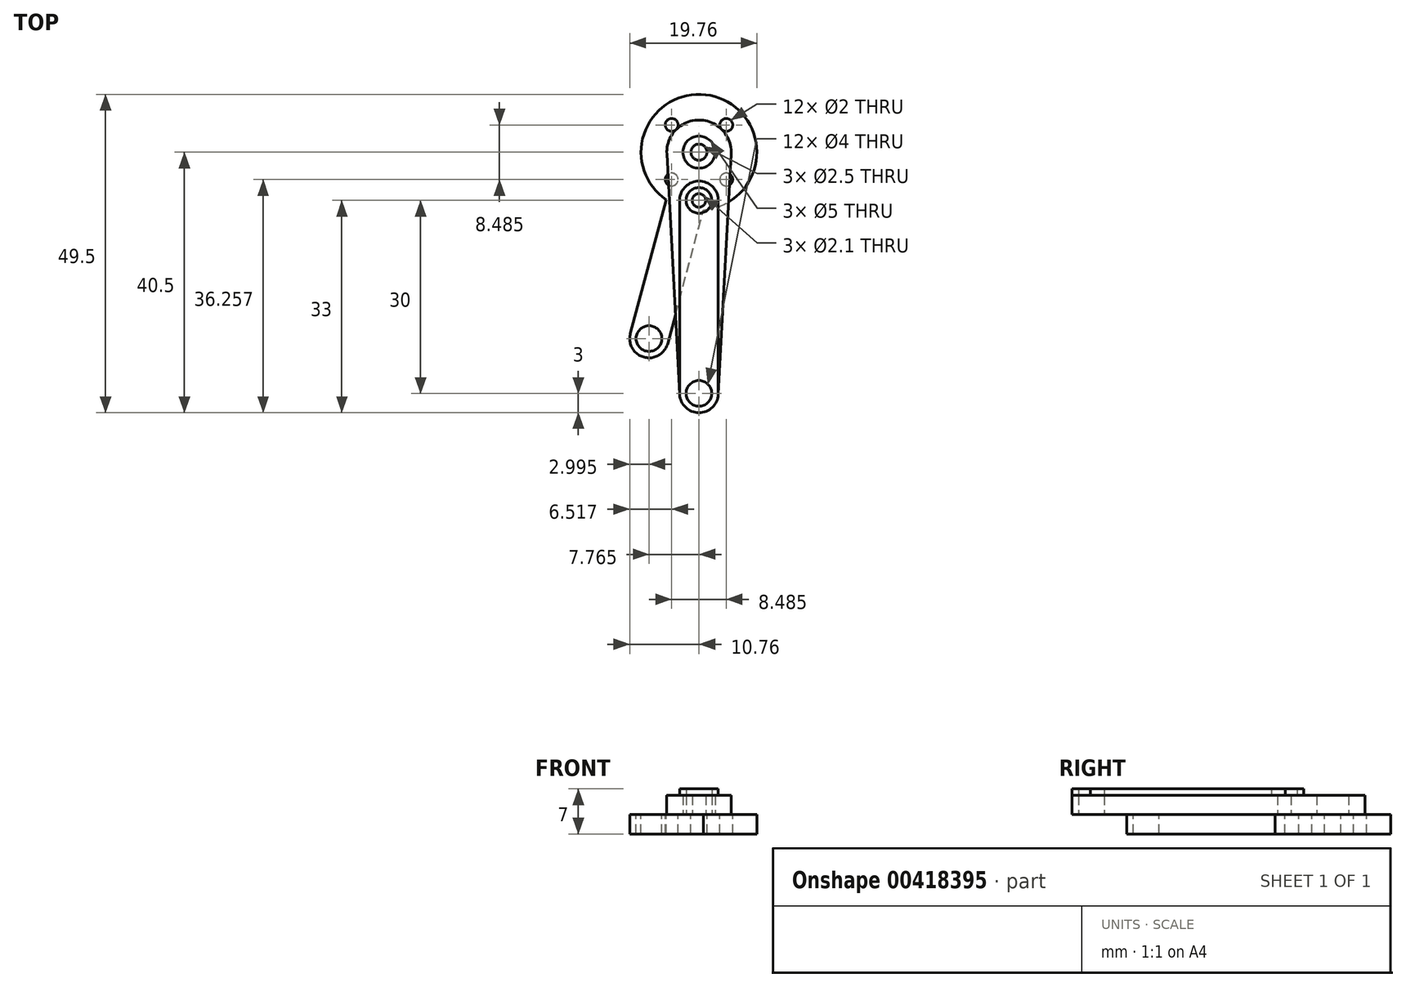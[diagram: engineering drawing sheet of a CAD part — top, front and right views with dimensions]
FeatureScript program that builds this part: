
annotation { "Feature Type Name" : "Feature", "Feature Type Description" : "" }
export const myFeature = defineFeature(function(context is Context, id is Id, definition is map)
    precondition{}
    {
        {
            var Q0;
            Q0=qCreatedBy(makeId("Top.planeOp"),FACE);
            var sketch = newSketch(context, id + "F0", { "sketchPlane" : qUnion([Q0])});
            skArc(sketch, "E0", {"start": v(5, -0.27) * mm, "mid": v(0, 5) * mm, "end": v(-5, -0.27) * mm});
            skCircle(sketch, "E1", {"center": v(0, 0) * mm, "radius": 2.5 * mm});
            skPoint(sketch, "E2", {"position": v(2.5, 0) * mm});
            skPoint(sketch, "E3", {"position": v(5, 0) * mm});
            skArc(sketch, "E4", {"start": v(-3, -37.66) * mm, "mid": v(0, -40.5) * mm, "end": v(3, -37.66) * mm});
            skLineSegment(sketch, "E5", {"start": v(-5, -0.27) * mm, "end": v(-3, -37.66) * mm});
            skCircle(sketch, "E6", {"center": v(0, -37.5) * mm, "radius": 2 * mm});
            skLineSegment(sketch, "E7.MirrorCS", {"start": v(5, -0.27) * mm, "end": v(3, -37.66) * mm});
            skCircle(sketch, "E8", {"center": v(0, -7.5) * mm, "radius": 1.05 * mm});
            skSolve(sketch);
        }
        {
            var Q0;
            Q0=qSketchRegion(id+"F0",true);
            extrude(context, id + "F1", {"entities" : qUnion([Q0]), "depth" : 3 * mm});
        }
        {
            var Q0;
            Q0=makeQuery(id+"F1.opExtrude","CAP_FACE",FACE,{"disambiguationData":[OSD([sQuery(id+"F0.wireOp",EDGE,"E0"),sQuery(id+"F0.wireOp",EDGE,"E1"),sQuery(id+"F0.wireOp",EDGE,"E4"),sQuery(id+"F0.wireOp",EDGE,"E5"),sQuery(id+"F0.wireOp",EDGE,"E6"),sQuery(id+"F0.wireOp",EDGE,"E7.MirrorCS"),sQuery(id+"F0.wireOp",EDGE,"E8")])],"isStart":false});
            var sketch = newSketch(context, id + "F2", { "sketchPlane" : qUnion([Q0])});
            skCircle(sketch, "E9.0", {"center": v(0, -37.5) * mm, "radius": 2 * mm});
            skArc(sketch, "E10.0", {"start": v(-3, -37.66) * mm, "mid": v(0, -40.5) * mm, "end": v(3, -37.66) * mm});
            skCircle(sketch, "E11", {"center": v(0, -7.5) * mm, "radius": 2 * mm});
            skLineSegment(sketch, "E12", {"start": v(0, -7.5) * mm, "end": v(0, -37.5) * mm, "construction": true});
            skLineSegment(sketch, "E13", {"start": v(-3.8, -22.5) * mm, "end": v(3.8, -22.5) * mm, "construction": true});
            skPoint(sketch, "E13.startSnap0", {"position": v(0, -22.5) * mm});
            skArc(sketch, "E14.MirrorCS", {"start": v(-3, -7.34) * mm, "mid": v(0, -4.5) * mm, "end": v(3, -7.34) * mm});
            skLineSegment(sketch, "E15", {"start": v(-3, -7.34) * mm, "end": v(-3, -37.66) * mm});
            skLineSegment(sketch, "E16.MirrorCS", {"start": v(3, -7.34) * mm, "end": v(3, -37.66) * mm});
            skSolve(sketch);
        }
        {
            var Q0;
            Q0=qSketchRegion(id+"F2",true);
            extrude(context, id + "F3", {"entities" : qUnion([Q0]), "depth" : 1 * mm});
        }
        {
            var Q0;
            Q0=makeQuery(id+"F1.opExtrude","CAP_FACE",FACE,{"disambiguationData":[OSD([sQuery(id+"F0.wireOp",EDGE,"E0"),sQuery(id+"F0.wireOp",EDGE,"E1"),sQuery(id+"F0.wireOp",EDGE,"E4"),sQuery(id+"F0.wireOp",EDGE,"E5"),sQuery(id+"F0.wireOp",EDGE,"E6"),sQuery(id+"F0.wireOp",EDGE,"E7.MirrorCS"),sQuery(id+"F0.wireOp",EDGE,"E8")])],"isStart":true});
            var sketch = newSketch(context, id + "F4", { "sketchPlane" : qUnion([Q0])});
            skCircle(sketch, "E17", {"center": v(0, 0) * mm, "radius": 6 * mm, "construction": true});
            skLineSegment(sketch, "E18.bottom", {"start": v(4.24, -4.24) * mm, "end": v(-4.24, -4.24) * mm, "construction": true});
            skLineSegment(sketch, "E18.top", {"start": v(4.24, 4.24) * mm, "end": v(-4.24, 4.24) * mm, "construction": true});
            skLineSegment(sketch, "E18.left", {"start": v(4.24, -4.24) * mm, "end": v(4.24, 4.24) * mm, "construction": true});
            skLineSegment(sketch, "E18.right", {"start": v(-4.24, -4.24) * mm, "end": v(-4.24, 4.24) * mm, "construction": true});
            skCircle(sketch, "E19", {"center": v(4.24, -4.24) * mm, "radius": 1 * mm});
            skCircle(sketch, "E20.MirrorC", {"center": v(-4.24, -4.24) * mm, "radius": 1 * mm});
            skCircle(sketch, "E21.MirrorC", {"center": v(-4.24, 4.24) * mm, "radius": 1 * mm});
            skCircle(sketch, "E22.MirrorC", {"center": v(4.24, 4.24) * mm, "radius": 1 * mm});
            skCircle(sketch, "E23", {"center": v(0, 0) * mm, "radius": 1.25 * mm});
            skArc(sketch, "E24", {"start": v(-5.1, 7.42) * mm, "mid": v(2.33, -8.7) * mm, "end": v(0.7, 8.97) * mm});
            skCircle(sketch, "E25", {"center": v(-7.76, 28.98) * mm, "radius": 2 * mm});
            skLineSegment(sketch, "E26", {"start": v(0, 0) * mm, "end": v(-7.76, 28.98) * mm, "construction": true});
            skArc(sketch, "E27", {"start": v(-4.87, 29.75) * mm, "mid": v(-8.54, 31.88) * mm, "end": v(-10.66, 28.2) * mm});
            skLineSegment(sketch, "E28", {"start": v(-7.76, 28.98) * mm, "end": v(-10.66, 28.2) * mm, "construction": true});
            skLineSegment(sketch, "E29", {"start": v(-10.66, 28.2) * mm, "end": v(-5.1, 7.42) * mm});
            skLineSegment(sketch, "E30.MirrorCS", {"start": v(-4.87, 29.75) * mm, "end": v(0.7, 8.97) * mm});
            skCircle(sketch, "E31.0", {"center": v(0, 7.5) * mm, "radius": 2 * mm, "construction": true});
            skCircle(sketch, "E32.0", {"center": v(0, 37.5) * mm, "radius": 2 * mm, "construction": true});
            skLineSegment(sketch, "E33", {"start": v(0, 7.5) * mm, "end": v(0, 37.5) * mm, "construction": true});
            skSolve(sketch);
        }
        {
            var Q0;
            Q0=qSketchRegion(id+"F4",true);
            extrude(context, id + "F5", {"entities" : qUnion([Q0]), "depth" : 3 * mm});
        }
    });
